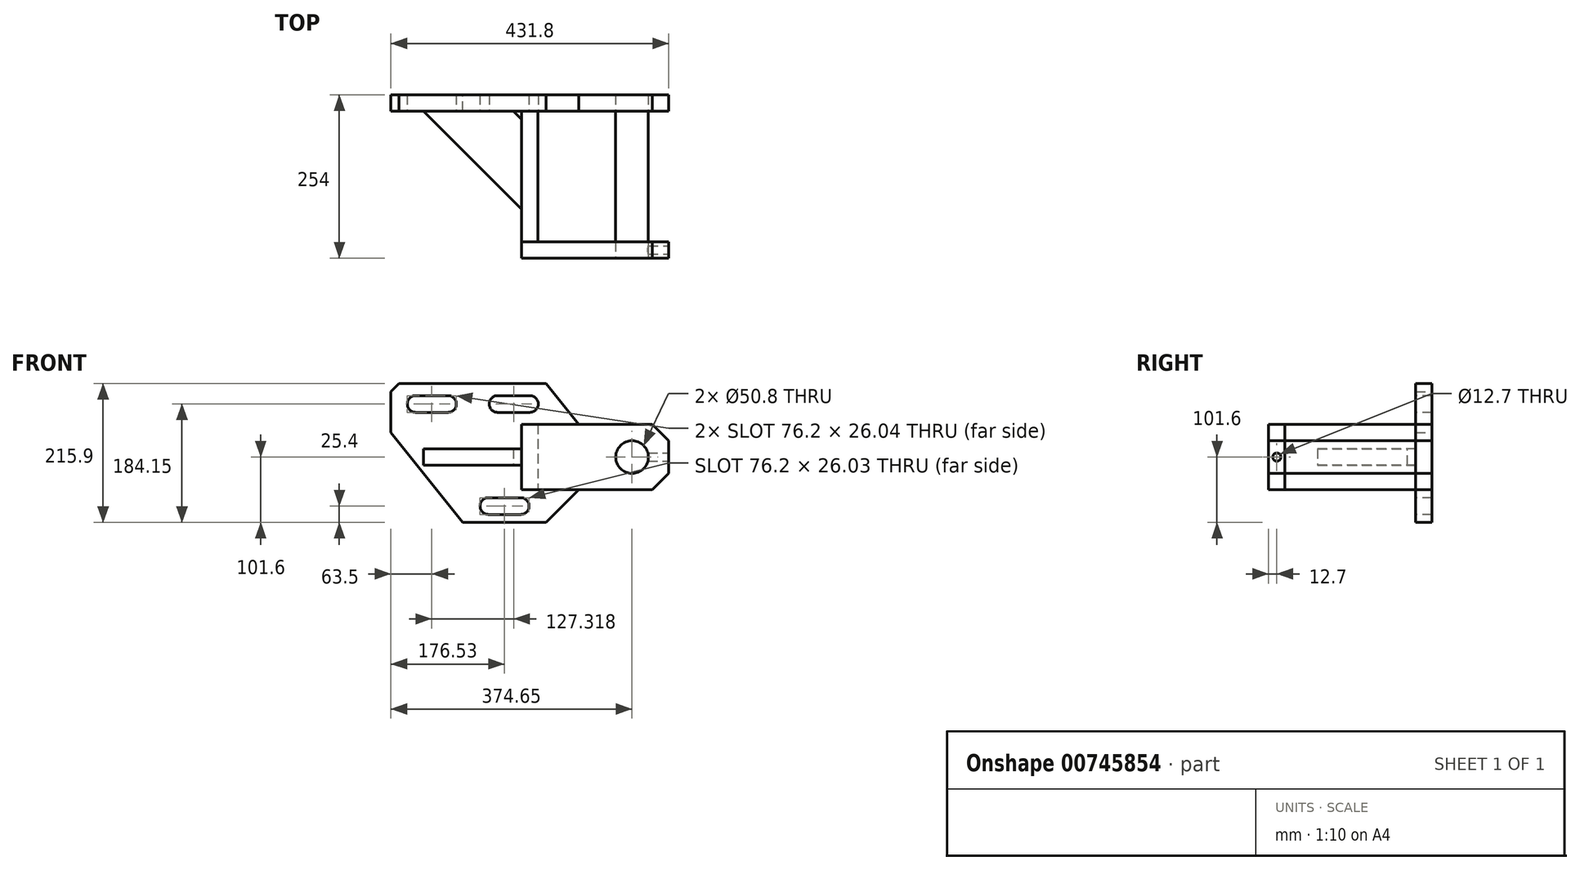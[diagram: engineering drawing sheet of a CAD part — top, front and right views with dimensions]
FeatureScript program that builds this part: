
annotation { "Feature Type Name" : "Feature", "Feature Type Description" : "" }
export const myFeature = defineFeature(function(context is Context, id is Id, definition is map)
    precondition{}
    {
        {
            var Q0;
            Q0=qCreatedBy(makeId("Front.planeOp"),FACE);
            var sketch = newSketch(context, id + "F0", { "sketchPlane" : qUnion([Q0])});
            skLineSegment(sketch, "E0", {"start": v(-215.9, 107.95) * mm, "end": v(25.4, 107.95) * mm});
            skLineSegment(sketch, "E1", {"start": v(25.4, 107.95) * mm, "end": v(76.2, 44.45) * mm});
            skLineSegment(sketch, "E2", {"start": v(76.2, 44.45) * mm, "end": v(215.9, 44.45) * mm});
            skLineSegment(sketch, "E3", {"start": v(215.9, 44.45) * mm, "end": v(215.9, -57.15) * mm});
            skLineSegment(sketch, "E4", {"start": v(215.9, -57.15) * mm, "end": v(76.2, -57.15) * mm});
            skLineSegment(sketch, "E5", {"start": v(76.2, -57.15) * mm, "end": v(25.4, -107.95) * mm});
            skLineSegment(sketch, "E6", {"start": v(25.4, -107.95) * mm, "end": v(-104.14, -107.95) * mm});
            skLineSegment(sketch, "E7", {"start": v(-104.14, -107.95) * mm, "end": v(-215.9, 31.75) * mm});
            skLineSegment(sketch, "E8", {"start": v(-215.9, 31.75) * mm, "end": v(-215.9, 107.95) * mm});
            skLineSegment(sketch, "E9", {"start": v(-104.14, -107.95) * mm, "end": v(-104.14, 107.95) * mm, "construction": true});
            skLineSegment(sketch, "E10", {"start": v(-215.9, 69.85) * mm, "end": v(215.9, 69.85) * mm, "construction": true});
            skPoint(sketch, "E11", {"position": v(-104.14, 0) * mm});
            skPoint(sketch, "E12", {"position": v(0, 69.85) * mm});
            skSolve(sketch);
        }
        {
            var Q0;
            Q0 = qSketchRegion(id + "F0", true);
            extrude(context, id + "F1", {"entities" : qUnion([Q0]), "depth" : 25.4 * mm, "offsetDistance" : 25.4 * mm});
        }
        {
            var Q0;
            Q0=makeQuery(id+"F1.opExtrude","CAP_FACE",FACE,{"disambiguationData":[OSD([sQuery(id+"F0.wireOp",EDGE,"E0"),sQuery(id+"F0.wireOp",EDGE,"E1"),sQuery(id+"F0.wireOp",EDGE,"E2"),sQuery(id+"F0.wireOp",EDGE,"E3"),sQuery(id+"F0.wireOp",EDGE,"E4"),sQuery(id+"F0.wireOp",EDGE,"E5"),sQuery(id+"F0.wireOp",EDGE,"E6"),sQuery(id+"F0.wireOp",EDGE,"E7"),sQuery(id+"F0.wireOp",EDGE,"E8")])],"isStart":false});
            var sketch = newSketch(context, id + "F2", { "sketchPlane" : qUnion([Q0])});
            skCircle(sketch, "E13", {"center": v(158.75, -6.35) * mm, "radius": 25.4 * mm});
            skPoint(sketch, "E13.centerSnap0", {"position": v(215.9, -6.35) * mm});
            skSolve(sketch);
        }
        {
            var Q0;
            Q0=makeQuery(id+"F2.imprint","IMPRINT",FACE,{"disambiguationData":[TD([[makeQuery(id+"F2.imprint","IMPRINT",EDGE,{"derivedFrom":sQuery(id+"F2.wireOp",EDGE,"E13")}),1.0]])]});
            extrude(context, id + "F3", {"entities" : qUnion([Q0]), "operationType" : NewBodyOperationType.REMOVE, "oppositeDirection" : true, "depth" : 25.4 * mm, "offsetDistance" : 25.4 * mm});
        }
        {
            var Q0;
            Q0=makeQuery(id+"F1.opExtrude","CAP_FACE",FACE,{"disambiguationData":[OSD([sQuery(id+"F0.wireOp",EDGE,"E0"),sQuery(id+"F0.wireOp",EDGE,"E1"),sQuery(id+"F0.wireOp",EDGE,"E2"),sQuery(id+"F0.wireOp",EDGE,"E3"),sQuery(id+"F0.wireOp",EDGE,"E4"),sQuery(id+"F0.wireOp",EDGE,"E5"),sQuery(id+"F0.wireOp",EDGE,"E6"),sQuery(id+"F0.wireOp",EDGE,"E7"),sQuery(id+"F0.wireOp",EDGE,"E8")])],"isStart":false});
            var sketch = newSketch(context, id + "F4", { "sketchPlane" : qUnion([Q0])});
            skLineSegment(sketch, "E14.bottom", {"start": v(-12.7, 44.45) * mm, "end": v(12.7, 44.45) * mm});
            skLineSegment(sketch, "E14.top", {"start": v(-12.7, -57.15) * mm, "end": v(12.7, -57.15) * mm});
            skLineSegment(sketch, "E14.left", {"start": v(-12.7, 44.45) * mm, "end": v(-12.7, -57.15) * mm});
            skLineSegment(sketch, "E14.right", {"start": v(12.7, 44.45) * mm, "end": v(12.7, -57.15) * mm});
            skPoint(sketch, "E15", {"position": v(12.7, -6.35) * mm});
            skSolve(sketch);
        }
        {
            var Q0;
            Q0=makeQuery(id+"F4.imprint","IMPRINT",FACE,{"disambiguationData":[TD([[makeQuery(id+"F4.imprint","IMPRINT",EDGE,{"derivedFrom":sQuery(id+"F4.wireOp",EDGE,"E14.bottom")}),-1.0]])]});
            extrude(context, id + "F5", {"entities" : qUnion([Q0]), "depth" : 203.2 * mm, "offsetDistance" : 25.4 * mm});
        }
        {
            var Q0;
            Q0=makeQuery(id+"F5.opExtrude","CAP_FACE",FACE,{"disambiguationData":[OSD([sQuery(id+"F4.wireOp",EDGE,"E14.bottom"),sQuery(id+"F4.wireOp",EDGE,"E14.top"),sQuery(id+"F4.wireOp",EDGE,"E14.left"),sQuery(id+"F4.wireOp",EDGE,"E14.right")])],"isStart":false});
            var sketch = newSketch(context, id + "F6", { "sketchPlane" : qUnion([Q0])});
            skLineSegment(sketch, "E16.bottom", {"start": v(-12.7, -57.15) * mm, "end": v(215.9, -57.15) * mm});
            skLineSegment(sketch, "E16.top", {"start": v(-12.7, 44.45) * mm, "end": v(215.9, 44.45) * mm});
            skLineSegment(sketch, "E16.left", {"start": v(-12.7, -57.15) * mm, "end": v(-12.7, 44.45) * mm});
            skLineSegment(sketch, "E16.right", {"start": v(215.9, -57.15) * mm, "end": v(215.9, 44.45) * mm});
            skSolve(sketch);
        }
        {
            var Q0;
            Q0 = qSketchRegion(id + "F6", true);
            extrude(context, id + "F7", {"entities" : qUnion([Q0]), "depth" : 25.4 * mm, "offsetDistance" : 25.4 * mm});
        }
        {
            var Q0;
            {var subQ0=sQuery(id+"F6.wireOp",EDGE,"E16.top");var subQ1=sQuery(id+"F6.wireOp",EDGE,"E16.bottom");var subQ2=sQuery(id+"F4.wireOp",EDGE,"E14.right");Q0=makeQuery(id+"F1RTuM7nUw5yEnr_4.opBoolean","MERGE",FACE,{"derivedFrom":[makeQuery(id+"F7.opExtrude","CAP_FACE",FACE,{"disambiguationData":[OSD([subQ2,subQ1,subQ0,sQuery(id+"F6.wireOp",EDGE,"E16.left")])],"isStart":false}),makeQuery(id+"F7.opExtrude","CAP_FACE",FACE,{"disambiguationData":[OSD([subQ2,subQ1,subQ0,sQuery(id+"F6.wireOp",EDGE,"E16.right")])],"isStart":false})]});}
            var sketch = newSketch(context, id + "F8", { "sketchPlane" : qUnion([Q0])});
            skCircle(sketch, "E17", {"center": v(158.75, -6.35) * mm, "radius": 25.4 * mm});
            skPoint(sketch, "E17.centerSnap0", {"position": v(215.9, -6.35) * mm});
            skSolve(sketch);
        }
        {
            var Q0;
            Q0=makeQuery(id+"F8.imprint","IMPRINT",FACE,{"disambiguationData":[TD([[makeQuery(id+"F8.imprint","IMPRINT",EDGE,{"derivedFrom":sQuery(id+"F8.wireOp",EDGE,"E17")}),1.0]])]});
            extrude(context, id + "F9", {"entities" : qUnion([Q0]), "operationType" : NewBodyOperationType.REMOVE, "oppositeDirection" : true, "depth" : 25.4 * mm, "offsetDistance" : 25.4 * mm});
        }
        {
            var Q0;
            Q0=makeQuery(id+"F5.opExtrude","SWEPT_FACE",FACE,{"disambiguationData":[OSD([sQuery(id+"F4.wireOp",EDGE,"E14.bottom")])]});
            var Q1;
            Q1=makeQuery(id+"F5.opExtrude","SWEPT_FACE",FACE,{"disambiguationData":[OSD([sQuery(id+"F4.wireOp",EDGE,"E14.top")])]});
            cPlane(context, id + "F10", {"entities" : qUnion([Q0, Q1]), "cplaneType" : CPlaneType.MID_PLANE, "offset" : 25.4 * mm, "width" : 152.4 * mm, "height" : 152.4 * mm});
        }
        {
            var Q0;
            Q0=qCreatedBy(id+"F10.planeOp",FACE);
            var sketch = newSketch(context, id + "F11", { "sketchPlane" : qUnion([Q0])});
            skLineSegment(sketch, "E18", {"start": v(-165.1, -25.4) * mm, "end": v(-12.7, -177.8) * mm});
            skLineSegment(sketch, "E19", {"start": v(-12.7, -177.8) * mm, "end": v(-12.7, -25.4) * mm});
            skLineSegment(sketch, "E20", {"start": v(-12.7, -25.4) * mm, "end": v(-165.1, -25.4) * mm});
            skSolve(sketch);
        }
        {
            var Q0;
            Q0=makeQuery(id+"F11.imprint","IMPRINT",FACE,{"disambiguationData":[TD([[makeQuery(id+"F11.imprint","IMPRINT",EDGE,{"derivedFrom":sQuery(id+"F11.wireOp",EDGE,"E18")}),1.0]])]});
            extrude(context, id + "F12", {"entities" : qUnion([Q0]), "endBound" : BoundingType.SYMMETRIC, "depth" : 25.4 * mm, "offsetDistance" : 25.4 * mm});
        }
        {
            var Q0;
            Q0=makeQuery(id+"F12.opExtrude","SWEPT_EDGE",EDGE,{"disambiguationData":[OSD([sQuery(id+"F11.wireOp",EDGE,"E19"),sQuery(id+"F11.wireOp",EDGE,"E20")])]});
            chamfer(context, id + "F13", {"entities" : qUnion([Q0]), "width" : 12.7 * mm, "tangentPropagation" : true});
        }
        {
            var Q0;
            Q0=makeQuery(id+"F7.opExtrude","SWEPT_EDGE",EDGE,{"disambiguationData":[OSD([sQuery(id+"F6.wireOp",EDGE,"E16.top"),sQuery(id+"F6.wireOp",EDGE,"E16.right")])]});
            var Q1;
            Q1=makeQuery(id+"F7.opExtrude","SWEPT_EDGE",EDGE,{"disambiguationData":[OSD([sQuery(id+"F6.wireOp",EDGE,"E16.bottom"),sQuery(id+"F6.wireOp",EDGE,"E16.right")])]});
            var Q2;
            Q2=makeQuery(id+"F1.opExtrude","SWEPT_EDGE",EDGE,{"disambiguationData":[OSD([sQuery(id+"F0.wireOp",EDGE,"E3"),sQuery(id+"F0.wireOp",EDGE,"E4")])]});
            var Q3;
            Q3=makeQuery(id+"F1.opExtrude","SWEPT_EDGE",EDGE,{"disambiguationData":[OSD([sQuery(id+"F0.wireOp",EDGE,"E2"),sQuery(id+"F0.wireOp",EDGE,"E3")])]});
            chamfer(context, id + "F14", {"entities" : qUnion([Q0, Q1, Q2, Q3]), "width" : 25.4 * mm, "tangentPropagation" : true});
        }
        {
            var Q0;
            Q0=makeQuery(id+"F1.opExtrude","SWEPT_EDGE",EDGE,{"disambiguationData":[OSD([sQuery(id+"F0.wireOp",EDGE,"E0"),sQuery(id+"F0.wireOp",EDGE,"E8")])]});
            chamfer(context, id + "F15", {"entities" : qUnion([Q0]), "width" : 12.7 * mm, "tangentPropagation" : true});
        }
        {
            var Q0;
            Q0 = qSketchRegion(id + "F8", true);
            var Q1;
            Q1=makeQuery(id+"F1.opExtrude","CAP_FACE",FACE,{"disambiguationData":[OSD([sQuery(id+"F0.wireOp",EDGE,"E0"),sQuery(id+"F0.wireOp",EDGE,"E1"),sQuery(id+"F0.wireOp",EDGE,"E2"),sQuery(id+"F0.wireOp",EDGE,"E3"),sQuery(id+"F0.wireOp",EDGE,"E4"),sQuery(id+"F0.wireOp",EDGE,"E5"),sQuery(id+"F0.wireOp",EDGE,"E6"),sQuery(id+"F0.wireOp",EDGE,"E7"),sQuery(id+"F0.wireOp",EDGE,"E8")])],"isStart":true});
            extrude(context, id + "F16", {"entities" : qUnion([Q0]), "endBound" : BoundingType.UP_TO_SURFACE, "oppositeDirection" : true, "depth" : 25.4 * mm, "endBoundEntityFace" : qUnion([Q1]), "offsetDistance" : 25.4 * mm});
        }
        {
            var Q0;
            Q0=makeQuery(id+"F7.opExtrude","SWEPT_FACE",FACE,{"disambiguationData":[OSD([sQuery(id+"F6.wireOp",EDGE,"E16.right")])]});
            var sketch = newSketch(context, id + "F17", { "sketchPlane" : qUnion([Q0])});
            skCircle(sketch, "E21", {"center": v(-241.3, -6.35) * mm, "radius": 6.35 * mm});
            skPoint(sketch, "E21.centerSnap0", {"position": v(-241.3, 19.05) * mm});
            skPoint(sketch, "E21.centerSnap1", {"position": v(-228.6, -6.35) * mm});
            skSolve(sketch);
        }
        {
            var Q0;
            Q0=makeQuery(id+"F17.imprint","IMPRINT",FACE,{"disambiguationData":[TD([[makeQuery(id+"F17.imprint","IMPRINT",EDGE,{"derivedFrom":sQuery(id+"F17.wireOp",EDGE,"E21")}),1.0]])]});
            extrude(context, id + "F18", {"entities" : qUnion([Q0]), "operationType" : NewBodyOperationType.REMOVE, "endBound" : BoundingType.UP_TO_NEXT, "oppositeDirection" : true, "depth" : 25.4 * mm, "offsetDistance" : 25.4 * mm});
        }
        {
            var Q0;
            Q0=makeQuery(id+"F1.opExtrude","CAP_FACE",FACE,{"disambiguationData":[OSD([sQuery(id+"F0.wireOp",EDGE,"E0"),sQuery(id+"F0.wireOp",EDGE,"E1"),sQuery(id+"F0.wireOp",EDGE,"E2"),sQuery(id+"F0.wireOp",EDGE,"E3"),sQuery(id+"F0.wireOp",EDGE,"E4"),sQuery(id+"F0.wireOp",EDGE,"E5"),sQuery(id+"F0.wireOp",EDGE,"E6"),sQuery(id+"F0.wireOp",EDGE,"E7"),sQuery(id+"F0.wireOp",EDGE,"E8")])],"isStart":false});
            var sketch = newSketch(context, id + "F19", { "sketchPlane" : qUnion([Q0])});
            skLineSegment(sketch, "E22", {"start": v(-177.48, 89.22) * mm, "end": v(-127.32, 89.22) * mm});
            skArc(sketch, "E23", {"start": v(-127.32, 63.18) * mm, "mid": v(-114.3, 76.2) * mm, "end": v(-127.32, 89.22) * mm});
            skLineSegment(sketch, "E24", {"start": v(-127.32, 63.18) * mm, "end": v(-177.48, 63.18) * mm});
            skArc(sketch, "E25", {"start": v(-177.48, 89.22) * mm, "mid": v(-190.5, 76.2) * mm, "end": v(-177.48, 63.18) * mm});
            skLineSegment(sketch, "E26", {"start": v(-50.16, 89.22) * mm, "end": v(0, 89.22) * mm});
            skArc(sketch, "E27", {"start": v(0, 63.18) * mm, "mid": v(13.02, 76.2) * mm, "end": v(0, 89.22) * mm});
            skLineSegment(sketch, "E28", {"start": v(0, 63.18) * mm, "end": v(-50.17, 63.18) * mm});
            skArc(sketch, "E29", {"start": v(-50.16, 89.22) * mm, "mid": v(-63.18, 76.2) * mm, "end": v(-50.17, 63.18) * mm});
            skLineSegment(sketch, "E30", {"start": v(-64.45, -69.53) * mm, "end": v(-14.29, -69.53) * mm});
            skArc(sketch, "E31", {"start": v(-14.29, -95.57) * mm, "mid": v(-1.27, -82.55) * mm, "end": v(-14.29, -69.53) * mm});
            skLineSegment(sketch, "E32", {"start": v(-14.29, -95.57) * mm, "end": v(-64.45, -95.57) * mm});
            skArc(sketch, "E33", {"start": v(-64.45, -69.53) * mm, "mid": v(-77.47, -82.55) * mm, "end": v(-64.45, -95.57) * mm});
            skLineSegment(sketch, "E34", {"start": v(-64.45, -82.55) * mm, "end": v(-14.29, -82.55) * mm, "construction": true});
            skPoint(sketch, "E35", {"position": v(-39.37, -95.57) * mm});
            skSolve(sketch);
        }
        {
            var Q0;
            Q0=makeQuery(id+"F19.imprint","IMPRINT",FACE,{"disambiguationData":[TD([[makeQuery(id+"F19.imprint","IMPRINT",EDGE,{"derivedFrom":sQuery(id+"F19.wireOp",EDGE,"E22")}),-1.0]])]});
            var Q1;
            Q1=makeQuery(id+"F19.imprint","IMPRINT",FACE,{"disambiguationData":[TD([[makeQuery(id+"F19.imprint","IMPRINT",EDGE,{"derivedFrom":sQuery(id+"F19.wireOp",EDGE,"E26")}),-1.0]])]});
            var Q2;
            Q2=makeQuery(id+"F19.imprint","IMPRINT",FACE,{"disambiguationData":[TD([[makeQuery(id+"F19.imprint","IMPRINT",EDGE,{"derivedFrom":sQuery(id+"F19.wireOp",EDGE,"E30")}),-1.0]])]});
            extrude(context, id + "F20", {"entities" : qUnion([Q0, Q1, Q2]), "operationType" : NewBodyOperationType.REMOVE, "oppositeDirection" : true, "depth" : 25.4 * mm, "offsetDistance" : 25.4 * mm});
        }
    });
